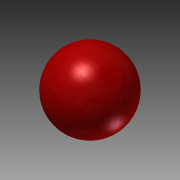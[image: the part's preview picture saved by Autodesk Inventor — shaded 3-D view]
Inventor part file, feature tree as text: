
AUTODESK INVENTOR PART (.ipt)
format: ipt  version: 2014 (Build 180170000, 170)  size: 135,680 bytes
history: native  units: in
note: dims shown in document units (in); Inventor stores cm internally (conversion verified against a paired STEP export)
features: revolve x1, sketch x1
ambient origin geometry x8: Origin, YZ Plane, XZ Plane, XY Plane, X Axis, Y Axis, Z Axis, Center Point
bodies: Solid1 (feature_tree)
feature tree (2):
  revolve  "Revolution1"  [1 undecoded]
  sketch  "Sketch1"  dims[d0=24.0in d1=0.125in d2=90.0deg]
note: 1 required parameter value undecoded (feature->parameter linkage not recoverable at this tier; creation-order binding heuristic only, values carry confidence <= 0.55)
